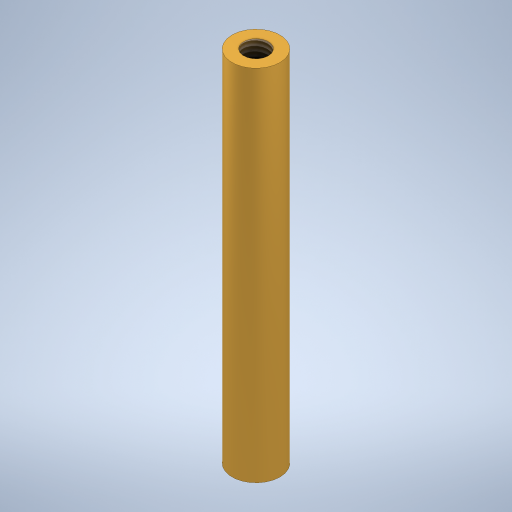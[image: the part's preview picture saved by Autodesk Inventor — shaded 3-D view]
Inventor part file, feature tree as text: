
AUTODESK INVENTOR PART (.ipt)
format: ipt  version: 2023 (Build 270158000, 158)  size: 260,608 bytes
history: native  units: mm
features: hole x2, sketch x2, other x1, extrude x1
ambient origin geometry x8: Origin, YZ Plane, XZ Plane, XY Plane, X Axis, Y Axis, Z Axis, Center Point
bodies: Body1 (feature_tree)
feature tree (6):
  other  "Sólido1"
  extrude  "Extrusão1"  Depth=60.0mm TaperAngle=0.0deg
  hole  "Furo1"  [1 undecoded]
  hole  "Furo2"  [1 undecoded]
  sketch  "Esboço4"  dims[d1=8.0mm d2=60.0mm d3=0.0mm]
  sketch  "Esboço5"  dims[d14=4.134mm d15=10.0mm d16=3.023mm d17=2.0mm d18=14.3117mm d19=14.2mm d20=20.594885mm d21=4.134mm d22=10.0mm d23=4.0mm d24=2.0mm d25=90.0deg d26=14.2mm d27=20.594885mm d10=0.5mm d11=0.872665mm d12=0.5mm d13=0.872665mm]
note: 2 required parameter values undecoded (feature->parameter linkage not recoverable at this tier; creation-order binding heuristic only, values carry confidence <= 0.55)
